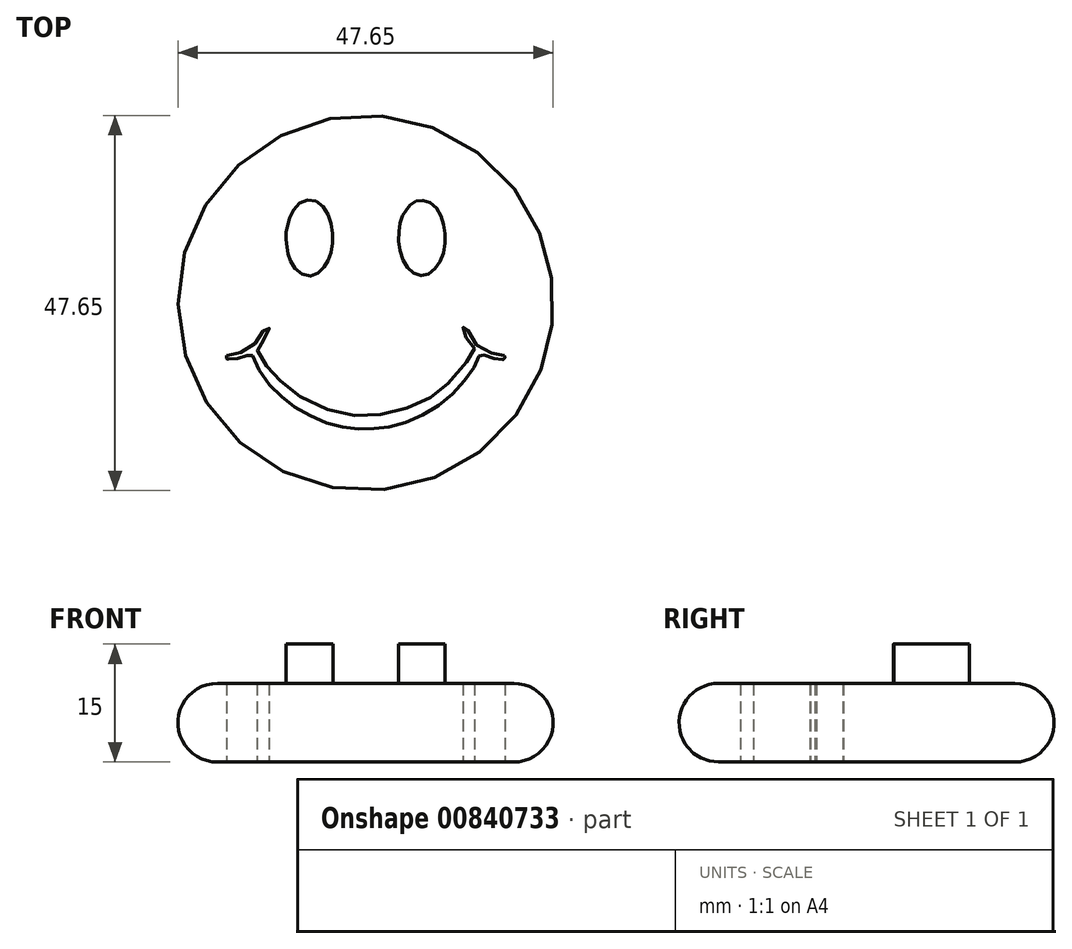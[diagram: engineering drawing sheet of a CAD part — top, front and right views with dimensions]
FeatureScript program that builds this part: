
annotation { "Feature Type Name" : "Feature", "Feature Type Description" : "" }
export const myFeature = defineFeature(function(context is Context, id is Id, definition is map)
    precondition{}
    {
        {
            var Q0;
            Q0=qCreatedBy(makeId("Top.planeOp"),FACE);
            var sketch = newSketch(context, id + "F0", { "sketchPlane" : qUnion([Q0])});
            skCircle(sketch, "E0", {"center": v(12.97, -1.56) * mm, "radius": 23.83 * mm});
            skPoint(sketch, "E0.first.point", {"position": v(6.96, 21.5) * mm});
            skPoint(sketch, "E0.second.point", {"position": v(-10.43, -6) * mm});
            skPoint(sketch, "E0.third.point", {"position": v(26.11, -21.43) * mm});
            skSolve(sketch);
        }
        {
            var Q0;
            Q0 = qSketchRegion(id + "F0", true);
            extrude(context, id + "F1", {"entities" : qUnion([Q0]), "depth" : 10 * mm, "offsetDistance" : 25 * mm});
        }
        {
            var Q0;
            Q0=qCreatedBy(makeId("Top.planeOp"),FACE);
            var sketch = newSketch(context, id + "F2", { "sketchPlane" : qUnion([Q0])});
            skFitSpline(sketch, "E1", {"points": [v(3.04, 8.23) * mm, v(2.86, 7.13) * mm, v(3.01, 5.52) * mm, v(3.29, 4.17) * mm, v(4.27, 2.6) * mm, v(6.08, 1.85) * mm, v(7.57, 2.9) * mm, v(8.41, 4.3) * mm, v(8.83, 6.64) * mm, v(8.4, 9.23) * mm, v(7.14, 11.12) * mm, v(5.23, 11.45) * mm, v(3.71, 10.1) * mm, v(3.04, 8.23) * mm]});
            skSolve(sketch);
        }
        {
            var Q0;
            Q0 = qSketchRegion(id + "F2", true);
            extrude(context, id + "F3", {"entities" : qUnion([Q0]), "operationType" : NewBodyOperationType.ADD, "depth" : 15 * mm, "offsetDistance" : 25 * mm});
        }
        {
            var Q0;
            Q0=qCreatedBy(makeId("Top.planeOp"),FACE);
            var sketch = newSketch(context, id + "F4", { "sketchPlane" : qUnion([Q0])});
            skFitSpline(sketch, "E2", {"points": [v(17.7, 9.56) * mm, v(17.31, 8.3) * mm, v(17.17, 6.55) * mm, v(17.48, 4.62) * mm, v(18.24, 3.03) * mm, v(19.26, 2.15) * mm, v(20.5, 1.93) * mm, v(21.69, 2.65) * mm, v(22.56, 3.96) * mm, v(23.06, 5.8) * mm, v(23, 7.76) * mm, v(22.63, 9.33) * mm, v(21.8, 10.7) * mm, v(20.6, 11.42) * mm, v(19.65, 11.43) * mm, v(18.67, 10.95) * mm, v(18.13, 10.21) * mm, v(17.7, 9.56) * mm]});
            skSolve(sketch);
        }
        {
            var Q0;
            Q0 = qSketchRegion(id + "F4", true);
            extrude(context, id + "F5", {"entities" : qUnion([Q0]), "operationType" : NewBodyOperationType.ADD, "depth" : 15 * mm, "offsetDistance" : 25 * mm});
        }
        {
            var Q0;
            Q0=qCreatedBy(makeId("Top.planeOp"),FACE);
            var sketch = newSketch(context, id + "F6", { "sketchPlane" : qUnion([Q0])});
            skFitSpline(sketch, "E3", {"points": [v(26.83, -7.42) * mm, v(26.45, -7.05) * mm, v(25.66, -5.84) * mm, v(25.37, -5.02) * mm, v(25.35, -4.64) * mm, v(25.58, -4.55) * mm, v(25.84, -4.69) * mm, v(25.97, -5.1) * mm, v(26.85, -6.65) * mm, v(27.82, -7.4) * mm, v(29.7, -8.12) * mm, v(30.42, -8.13) * mm, v(30.67, -8.45) * mm, v(30.37, -8.75) * mm, v(29.6, -8.66) * mm, v(28.37, -8.39) * mm, v(27.63, -7.96) * mm, v(27.31, -8.57) * mm, v(26.19, -10.61) * mm, v(23.67, -13.43) * mm, v(20.44, -15.7) * mm, v(16.75, -17.12) * mm, v(13.94, -17.53) * mm, v(11.05, -17.45) * mm, v(7.93, -16.74) * mm, v(4.48, -15.07) * mm, v(1.87, -13.05) * mm, v(-0.44, -10.23) * mm, v(-1.57, -7.99) * mm, v(-1.94, -8.1) * mm, v(-2.96, -8.58) * mm, v(-4.1, -8.67) * mm, v(-4.61, -8.67) * mm, v(-4.7, -8.37) * mm, v(-4.43, -8.06) * mm, v(-3.12, -7.9) * mm, v(-1.53, -7.1) * mm, v(-0.46, -6) * mm, v(0, -5.02) * mm, v(0.29, -4.54) * mm, v(0.72, -4.75) * mm, v(0.63, -5.13) * mm, v(0, -6.26) * mm, v(-0.82, -7.35) * mm, v(-0.71, -7.65) * mm, v(0.2, -9.28) * mm, v(1.74, -11.03) * mm, v(4.35, -13.27) * mm, v(9.18, -15.38) * mm, v(13.12, -15.9) * mm, v(17.34, -15.2) * mm, v(21, -13.7) * mm, v(23.38, -11.84) * mm, v(26.21, -8.51) * mm, v(26.83, -7.42) * mm]});
            skSolve(sketch);
        }
        {
            var Q0;
            Q0 = qSketchRegion(id + "F6", true);
            extrude(context, id + "F7", {"entities" : qUnion([Q0]), "operationType" : NewBodyOperationType.REMOVE, "depth" : 42.7 * mm, "offsetDistance" : 25 * mm});
        }
        {
            var Q0;
            Q0=makeQuery(id+"F1.opExtrude","CAP_EDGE",EDGE,{"disambiguationData":[OSD([sQuery(id+"F0.wireOp",EDGE,"E0")])],"isStart":false});
            var Q1;
            Q1=makeQuery(id+"F1.opExtrude","CAP_EDGE",EDGE,{"disambiguationData":[OSD([sQuery(id+"F0.wireOp",EDGE,"E0")])],"isStart":true});
            fillet(context, id + "F8", {"entities" : qUnion([Q0, Q1]), "radius" : 5 * mm, "tangentPropagation" : true, "allowEdgeOverflow" : false});
        }
    });
